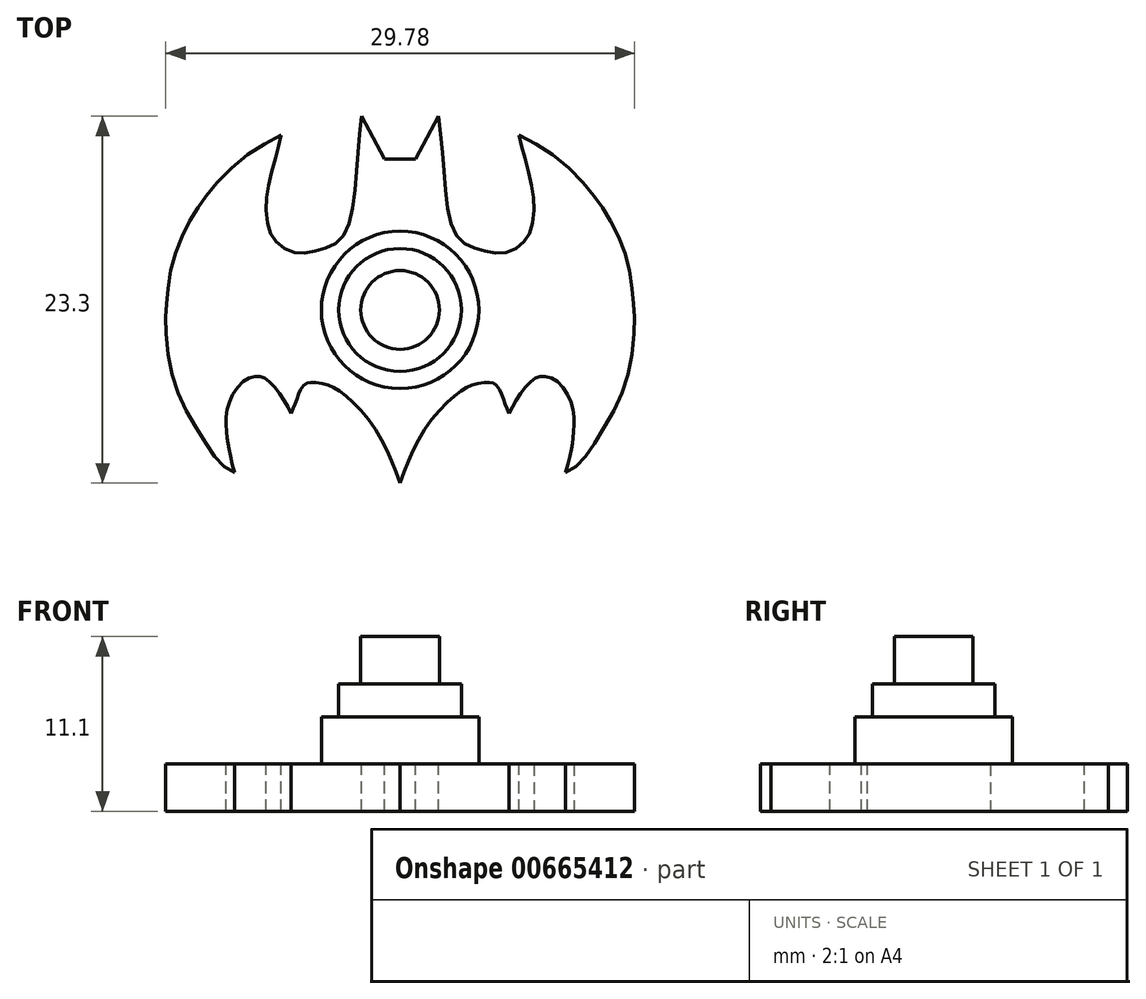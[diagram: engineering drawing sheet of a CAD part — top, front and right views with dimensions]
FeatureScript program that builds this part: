
annotation { "Feature Type Name" : "Feature", "Feature Type Description" : "" }
export const myFeature = defineFeature(function(context is Context, id is Id, definition is map)
    precondition{}
    {
        {
            var Q0;
            Q0=qCreatedBy(makeId("Top.planeOp"),FACE);
            var sketch = newSketch(context, id + "F0", { "sketchPlane" : qUnion([Q0])});
            skFitSpline(sketch, "E0", {"points": [v(0, -13.14) * mm, v(-1.56, -9.75) * mm, v(-3.7, -7.4) * mm, v(-4.68, -6.89) * mm, v(-5.61, -6.74) * mm, v(-6.04, -6.86) * mm, v(-6.39, -7.37) * mm, v(-6.64, -8.04) * mm, v(-6.93, -8.73) * mm], "startDerivative": vector(-5.93, 16.12) * mm, "endDerivative": vector(-3.07, -7.1) * mm});
            skFitSpline(sketch, "E1", {"points": [v(-6.93, -8.73) * mm, v(-7.58, -7.55) * mm, v(-8.5, -6.53) * mm, v(-9, -6.35) * mm, v(-9.85, -6.6) * mm, v(-10.76, -7.78) * mm, v(-11.06, -9.14) * mm, v(-10.98, -10.28) * mm, v(-10.88, -10.97) * mm, v(-10.52, -12.48) * mm], "startDerivative": vector(-4.6, 9.68) * mm, "endDerivative": vector(3.25, -12.82) * mm});
            skFitSpline(sketch, "E2", {"points": [v(-10.52, -12.48) * mm, v(-11.43, -11.87) * mm, v(-12.38, -10.55) * mm, v(-13.71, -8.27) * mm, v(-14.59, -5.78) * mm, v(-14.89, -2.97) * mm, v(-14.81, -1.67) * mm, v(-14.56, 0.42) * mm, v(-13.84, 2.55) * mm, v(-12.9, 4.27) * mm, v(-11.97, 5.54) * mm, v(-9.86, 7.6) * mm, v(-7.54, 8.95) * mm], "startDerivative": vector(-15.76, 8.46) * mm, "endDerivative": vector(24.77, 12.2) * mm});
            skFitSpline(sketch, "E3", {"points": [v(-7.54, 8.95) * mm, v(-7.86, 7.72) * mm, v(-8.34, 5.87) * mm, v(-8.5, 4.45) * mm, v(-8.32, 2.94) * mm, v(-7.86, 2.19) * mm, v(-6.93, 1.55) * mm, v(-5.88, 1.5) * mm, v(-4.82, 1.74) * mm, v(-3.8, 2.3) * mm, v(-3.1, 3.82) * mm, v(-2.76, 6.96) * mm, v(-2.44, 10.16) * mm], "startDerivative": vector(-3.77, -15.18) * mm, "endDerivative": vector(2.84, 26.23) * mm});
            skFitSpline(sketch, "E4", {"points": [v(-2.44, 10.16) * mm, v(-1, 7.44) * mm], "startDerivative": vector(1.45, -2.72) * mm, "endDerivative": vector(1.45, -2.72) * mm});
            skFitSpline(sketch, "E5", {"points": [v(-1, 7.44) * mm, v(0, 7.44) * mm], "startDerivative": vector(1, 0) * mm, "endDerivative": vector(1, 0) * mm});
            skFitSpline(sketch, "E6.MirrorCS", {"points": [v(2.44, 10.16) * mm, v(1, 7.44) * mm], "startDerivative": vector(-1.45, -2.72) * mm, "endDerivative": vector(-1.45, -2.72) * mm});
            skFitSpline(sketch, "E7.MirrorCS", {"points": [v(1, 7.44) * mm, v(0, 7.44) * mm], "startDerivative": vector(-1, 0) * mm, "endDerivative": vector(-1, 0) * mm});
            skFitSpline(sketch, "E8.MirrorCS", {"points": [v(0, -13.14) * mm, v(1.56, -9.75) * mm, v(3.7, -7.4) * mm, v(4.68, -6.89) * mm, v(5.61, -6.74) * mm, v(6.04, -6.86) * mm, v(6.39, -7.37) * mm, v(6.64, -8.04) * mm, v(6.93, -8.73) * mm], "startDerivative": vector(5.93, 16.12) * mm, "endDerivative": vector(3.07, -7.1) * mm});
            skFitSpline(sketch, "E9.MirrorCS", {"points": [v(6.93, -8.73) * mm, v(7.58, -7.55) * mm, v(8.5, -6.53) * mm, v(9, -6.35) * mm, v(9.85, -6.6) * mm, v(10.76, -7.78) * mm, v(11.06, -9.14) * mm, v(10.98, -10.28) * mm, v(10.88, -10.97) * mm, v(10.52, -12.48) * mm], "startDerivative": vector(4.6, 9.68) * mm, "endDerivative": vector(-3.25, -12.82) * mm});
            skFitSpline(sketch, "E10.MirrorCS", {"points": [v(7.54, 8.95) * mm, v(7.86, 7.72) * mm, v(8.34, 5.87) * mm, v(8.5, 4.45) * mm, v(8.32, 2.94) * mm, v(7.86, 2.19) * mm, v(6.93, 1.55) * mm, v(5.88, 1.5) * mm, v(4.82, 1.74) * mm, v(3.8, 2.3) * mm, v(3.1, 3.82) * mm, v(2.76, 6.96) * mm, v(2.44, 10.16) * mm], "startDerivative": vector(3.77, -15.18) * mm, "endDerivative": vector(-2.84, 26.23) * mm});
            skFitSpline(sketch, "E11.MirrorCS", {"points": [v(10.52, -12.48) * mm, v(11.43, -11.87) * mm, v(12.38, -10.55) * mm, v(13.71, -8.27) * mm, v(14.59, -5.78) * mm, v(14.89, -2.97) * mm, v(14.81, -1.67) * mm, v(14.56, 0.42) * mm, v(13.84, 2.55) * mm, v(12.9, 4.27) * mm, v(11.97, 5.54) * mm, v(9.86, 7.6) * mm, v(7.54, 8.95) * mm], "startDerivative": vector(15.76, 8.46) * mm, "endDerivative": vector(-24.77, 12.2) * mm});
            skLineSegment(sketch, "E12", {"start": v(0, -13.14) * mm, "end": v(0, -2.14) * mm, "construction": true});
            skCircle(sketch, "E13", {"center": v(0, -2.14) * mm, "radius": 5 * mm});
            skCircle(sketch, "E14", {"center": v(0, -2.14) * mm, "radius": 3.9 * mm});
            skSolve(sketch);
        }
        {
            var Q0;
            Q0=makeQuery(id+"F0.imprint","IMPRINT",FACE,{"disambiguationData":[TD([[makeQuery(id+"F0.imprint","IMPRINT",EDGE,{"derivedFrom":sQuery(id+"F0.wireOp",EDGE,"E13")}),1.0]])]});
            extrude(context, id + "F1", {"entities" : qUnion([Q0]), "depth" : 3 * mm, "offsetDistance" : 25 * mm});
        }
        {
            var Q0;
            Q0=makeQuery(id+"F0.imprint","IMPRINT",FACE,{"disambiguationData":[TD([[makeQuery(id+"F0.imprint","IMPRINT",EDGE,{"derivedFrom":sQuery(id+"F0.wireOp",EDGE,"E14")}),1.0]])]});
            extrude(context, id + "F2", {"entities" : qUnion([Q0]), "operationType" : NewBodyOperationType.ADD, "depth" : 5.1 * mm, "offsetDistance" : 25 * mm});
        }
        {
            var Q0;
            Q0=makeQuery(id+"F0.imprint","IMPRINT",FACE,{"disambiguationData":[TD([[makeQuery(id+"F0.imprint","IMPRINT",EDGE,{"derivedFrom":sQuery(id+"F0.wireOp",EDGE,"E0")}),-1.0]])]});
            var Q1;
            Q1=makeQuery(id+"F0.imprint","IMPRINT",FACE,{"disambiguationData":[TD([[makeQuery(id+"F0.imprint","IMPRINT",EDGE,{"derivedFrom":sQuery(id+"F0.wireOp",EDGE,"E14")}),1.0]])]});
            var Q2;
            Q2=makeQuery(id+"F0.imprint","IMPRINT",FACE,{"disambiguationData":[TD([[makeQuery(id+"F0.imprint","IMPRINT",EDGE,{"derivedFrom":sQuery(id+"F0.wireOp",EDGE,"E13")}),1.0]])]});
            extrude(context, id + "F3", {"entities" : qUnion([Q0, Q1, Q2]), "operationType" : NewBodyOperationType.ADD, "oppositeDirection" : true, "depth" : 3 * mm, "offsetDistance" : 25 * mm});
        }
        {
            var Q0;
            Q0=makeQuery(id+"F2.opExtrude","CAP_FACE",FACE,{"disambiguationData":[OSD([sQuery(id+"F0.wireOp",EDGE,"E14")])],"isStart":false});
            var sketch = newSketch(context, id + "F4", { "sketchPlane" : qUnion([Q0])});
            skCircle(sketch, "E15", {"center": v(0, -2.14) * mm, "radius": 2.5 * mm});
            skSolve(sketch);
        }
        {
            var Q0;
            Q0=makeQuery(id+"F4.imprint","IMPRINT",FACE,{"disambiguationData":[TD([[makeQuery(id+"F4.imprint","IMPRINT",EDGE,{"derivedFrom":sQuery(id+"F4.wireOp",EDGE,"E15")}),1.0]])]});
            extrude(context, id + "F5", {"entities" : qUnion([Q0]), "operationType" : NewBodyOperationType.ADD, "depth" : 3 * mm, "offsetDistance" : 25 * mm});
        }
    });
